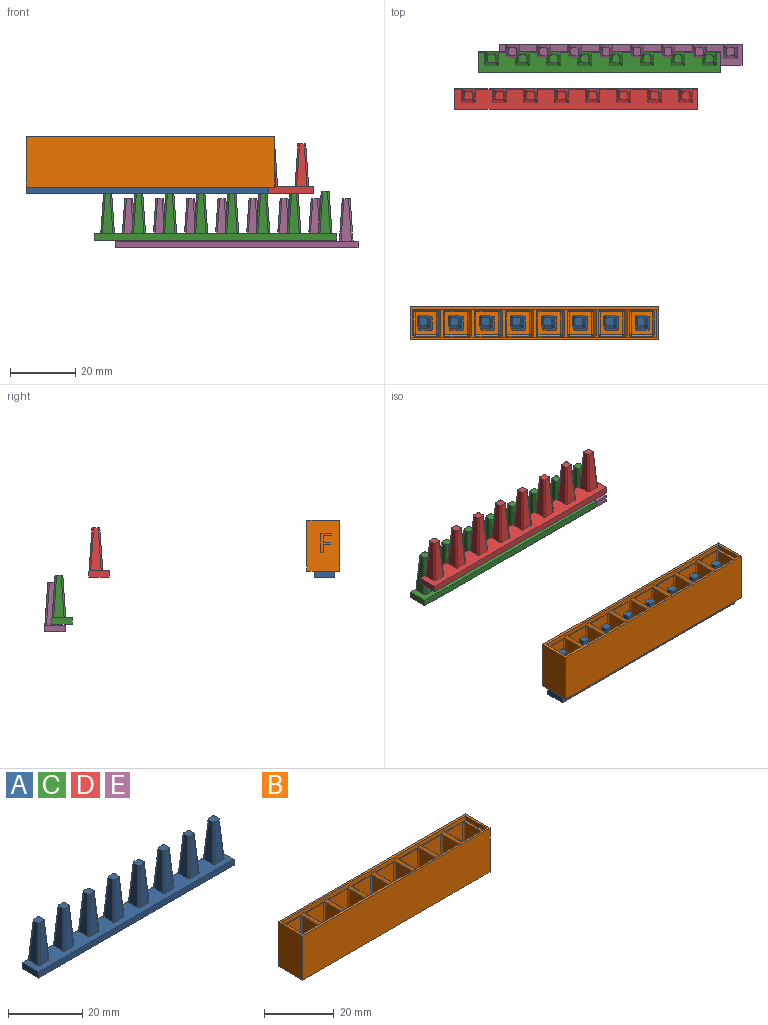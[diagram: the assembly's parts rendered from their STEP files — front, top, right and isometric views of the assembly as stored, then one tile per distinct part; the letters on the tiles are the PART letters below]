
ASSEMBLY  parts=5 mates=2
PART A: 78 faces, bbox 74.2x6.3x15 mm
  f0: plane 13x3.2mm, normal (-1,0,0.07), area 29.9mm2, adj f4,f5,f8,f9
  f1: plane 13x3.2mm, normal (0,-1,0.07), area 29.9mm2, adj f4,f5,f6,f9
  f2: plane 13x3.2mm, normal (1,0,0.07), area 29.9mm2, adj f4,f6,f7,f9
  f3: plane 13x3.2mm, normal (0,1,0.07), area 29.9mm2, adj f4,f7,f8,f74
  f4: plane 2.38x2.38mm, normal (0,0,1), area 5.5mm2, adj f0,f1,f2,f3,f5,f6,f7,f8
  f5: cylinder r=0.5mm len=13.03mm, axis (-0.07,-0.07,-1), area 10.2mm2, adj f0,f1,f4,f9
  f6: cylinder r=0.5mm len=13.03mm, axis (0.07,-0.07,-1), area 10.2mm2, adj f1,f2,f4,f9
  f7: cylinder r=0.5mm len=13.03mm, axis (0.07,0.07,-1), area 10.2mm2, adj f2,f3,f4,f9
  f8: cylinder r=0.5mm len=13.03mm, axis (-0.07,0.07,-1), area 10.2mm2, adj f0,f3,f4,f9
  f9: plane 74.2x6.2mm, normal (0,0,1), area 320.6mm2, adj f0,f1,f2,f5,f6,f7,f8,f11
  f10: plane 13x3.2mm, normal (0,1,0.07), area 29.9mm2, adj f14,f15,f18,f74
  f11: plane 13x3.2mm, normal (-1,0,0.07), area 29.9mm2, adj f9,f14,f15,f16
  f12: plane 13x3.2mm, normal (0,-1,0.07), area 29.9mm2, adj f9,f14,f16,f17
  f13: plane 13x3.2mm, normal (1,0,0.07), area 29.9mm2, adj f9,f14,f17,f18
  f14: plane 2.38x2.38mm, normal (0,0,1), area 5.5mm2, adj f10,f11,f12,f13,f15,f16,f17,f18
  f15: cylinder r=0.5mm len=13.03mm, axis (-0.07,0.07,-1), area 10.2mm2, adj f9,f10,f11,f14
  f16: cylinder r=0.5mm len=13.03mm, axis (-0.07,-0.07,-1), area 10.2mm2, adj f9,f11,f12,f14
  f17: cylinder r=0.5mm len=13.03mm, axis (0.07,-0.07,-1), area 10.2mm2, adj f9,f12,f13,f14
  f18: cylinder r=0.5mm len=13.03mm, axis (0.07,0.07,-1), area 10.2mm2, adj f9,f10,f13,f14
  f19: plane 13x3.2mm, normal (0,1,0.07), area 29.9mm2, adj f23,f24,f27,f74
  f20: plane 13x3.2mm, normal (-1,0,0.07), area 29.9mm2, adj f9,f23,f24,f25
  f21: plane 13x3.2mm, normal (0,-1,0.07), area 29.9mm2, adj f9,f23,f25,f26
  f22: plane 13x3.2mm, normal (1,0,0.07), area 29.9mm2, adj f9,f23,f26,f27
  f23: plane 2.38x2.38mm, normal (0,0,1), area 5.5mm2, adj f19,f20,f21,f22,f24,f25,f26,f27
  f24: cylinder r=0.5mm len=13.03mm, axis (-0.07,0.07,-1), area 10.2mm2, adj f9,f19,f20,f23
  f25: cylinder r=0.5mm len=13.03mm, axis (-0.07,-0.07,-1), area 10.2mm2, adj f9,f20,f21,f23
  f26: cylinder r=0.5mm len=13.03mm, axis (0.07,-0.07,-1), area 10.2mm2, adj f9,f21,f22,f23
  f27: cylinder r=0.5mm len=13.03mm, axis (0.07,0.07,-1), area 10.2mm2, adj f9,f19,f22,f23
  f28: plane 13x3.2mm, normal (0,1,0.07), area 29.9mm2, adj f32,f33,f36,f74
  f29: plane 13x3.2mm, normal (-1,0,0.07), area 29.9mm2, adj f9,f32,f33,f34
  f30: plane 13x3.2mm, normal (0,-1,0.07), area 29.9mm2, adj f9,f32,f34,f35
  f31: plane 13x3.2mm, normal (1,0,0.07), area 29.9mm2, adj f9,f32,f35,f36
  f32: plane 2.38x2.38mm, normal (0,0,1), area 5.5mm2, adj f28,f29,f30,f31,f33,f34,f35,f36
  f33: cylinder r=0.5mm len=13.03mm, axis (-0.07,0.07,-1), area 10.2mm2, adj f9,f28,f29,f32
  f34: cylinder r=0.5mm len=13.03mm, axis (-0.07,-0.07,-1), area 10.2mm2, adj f9,f29,f30,f32
  f35: cylinder r=0.5mm len=13.03mm, axis (0.07,-0.07,-1), area 10.2mm2, adj f9,f30,f31,f32
  f36: cylinder r=0.5mm len=13.03mm, axis (0.07,0.07,-1), area 10.2mm2, adj f9,f28,f31,f32
  f37: plane 13x3.2mm, normal (0,1,0.07), area 29.9mm2, adj f41,f42,f45,f74
  f38: plane 13x3.2mm, normal (-1,0,0.07), area 29.9mm2, adj f9,f41,f42,f43
  f39: plane 13x3.2mm, normal (0,-1,0.07), area 29.9mm2, adj f9,f41,f43,f44
  f40: plane 13x3.2mm, normal (1,0,0.07), area 29.9mm2, adj f9,f41,f44,f45
  f41: plane 2.38x2.38mm, normal (0,0,1), area 5.5mm2, adj f37,f38,f39,f40,f42,f43,f44,f45
  f42: cylinder r=0.5mm len=13.03mm, axis (-0.07,0.07,-1), area 10.2mm2, adj f9,f37,f38,f41
  f43: cylinder r=0.5mm len=13.03mm, axis (-0.07,-0.07,-1), area 10.2mm2, adj f9,f38,f39,f41
  f44: cylinder r=0.5mm len=13.03mm, axis (0.07,-0.07,-1), area 10.2mm2, adj f9,f39,f40,f41
  f45: cylinder r=0.5mm len=13.03mm, axis (0.07,0.07,-1), area 10.2mm2, adj f9,f37,f40,f41
  f46: plane 13x3.2mm, normal (0,1,0.07), area 29.9mm2, adj f50,f51,f54,f74
  f47: plane 13x3.2mm, normal (-1,0,0.07), area 29.9mm2, adj f9,f50,f51,f52
  f48: plane 13x3.2mm, normal (0,-1,0.07), area 29.9mm2, adj f9,f50,f52,f53
  f49: plane 13x3.2mm, normal (1,0,0.07), area 29.9mm2, adj f9,f50,f53,f54
  f50: plane 2.38x2.38mm, normal (0,0,1), area 5.5mm2, adj f46,f47,f48,f49,f51,f52,f53,f54
  f51: cylinder r=0.5mm len=13.03mm, axis (-0.07,0.07,-1), area 10.2mm2, adj f9,f46,f47,f50
  f52: cylinder r=0.5mm len=13.03mm, axis (-0.07,-0.07,-1), area 10.2mm2, adj f9,f47,f48,f50
  f53: cylinder r=0.5mm len=13.03mm, axis (0.07,-0.07,-1), area 10.2mm2, adj f9,f48,f49,f50
  f54: cylinder r=0.5mm len=13.03mm, axis (0.07,0.07,-1), area 10.2mm2, adj f9,f46,f49,f50
  f55: plane 13x3.2mm, normal (0,1,0.07), area 29.9mm2, adj f59,f60,f63,f74
  f56: plane 13x3.2mm, normal (-1,0,0.07), area 29.9mm2, adj f9,f59,f60,f61
  f57: plane 13x3.2mm, normal (0,-1,0.07), area 29.9mm2, adj f9,f59,f61,f62
  f58: plane 13x3.2mm, normal (1,0,0.07), area 29.9mm2, adj f9,f59,f62,f63
  f59: plane 2.38x2.38mm, normal (0,0,1), area 5.5mm2, adj f55,f56,f57,f58,f60,f61,f62,f63
  f60: cylinder r=0.5mm len=13.03mm, axis (-0.07,0.07,-1), area 10.2mm2, adj f9,f55,f56,f59
  f61: cylinder r=0.5mm len=13.03mm, axis (-0.07,-0.07,-1), area 10.2mm2, adj f9,f56,f57,f59
  f62: cylinder r=0.5mm len=13.03mm, axis (0.07,-0.07,-1), area 10.2mm2, adj f9,f57,f58,f59
  f63: cylinder r=0.5mm len=13.03mm, axis (0.07,0.07,-1), area 10.2mm2, adj f9,f55,f58,f59
  f64: plane 13x3.2mm, normal (0,1,0.07), area 29.9mm2, adj f68,f69,f72,f74
  f65: plane 13x3.2mm, normal (-1,0,0.07), area 29.9mm2, adj f9,f68,f69,f70
  f66: plane 13x3.2mm, normal (0,-1,0.07), area 29.9mm2, adj f9,f68,f70,f71
  f67: plane 13x3.2mm, normal (1,0,0.07), area 29.9mm2, adj f9,f68,f71,f72
  f68: plane 2.38x2.38mm, normal (0,0,1), area 5.5mm2, adj f64,f65,f66,f67,f69,f70,f71,f72
  f69: cylinder r=0.5mm len=13.03mm, axis (-0.07,0.07,-1), area 10.2mm2, adj f9,f64,f65,f68
  f70: cylinder r=0.5mm len=13.03mm, axis (-0.07,-0.07,-1), area 10.2mm2, adj f9,f65,f66,f68
  f71: cylinder r=0.5mm len=13.03mm, axis (0.07,-0.07,-1), area 10.2mm2, adj f9,f66,f67,f68
  f72: cylinder r=0.5mm len=13.03mm, axis (0.07,0.07,-1), area 10.2mm2, adj f9,f64,f67,f68
  f73: plane 6.34x2mm, normal (-1,0,0), area 12.5mm2, adj f9,f74,f76,f77
  f74: plane 74.2x2mm, normal (0,1,0.07), area 148.8mm2, adj f3,f9,f10,f19,f28,f37,f46,f55
  f75: plane 6.34x2mm, normal (1,0,0), area 12.5mm2, adj f9,f74,f76,f77
  f76: plane 74.2x2mm, normal (0,-1,0), area 148.4mm2, adj f9,f73,f75,f77
  f77: plane 74.2x6.34mm, normal (0,0,-1), area 470.4mm2, adj f73,f74,f75,f76
PART B: 255 faces, bbox 76x10x15.5 mm
  f0: plane 74.5x1.5mm, normal (0,1,0), area 108.2mm2, adj f1,f2,f3,f4,f5,f6,f7,f51
  f1: plane 8.5x8.09mm, normal (0,0,1), area 4.9mm2, adj f0,f21,f22,f23,f42,f213,f215,f218
  f2: plane 8.5x8.09mm, normal (0,0,1), area 4.9mm2, adj f0,f24,f25,f26,f43,f201,f203,f206
  f3: plane 8.5x8.09mm, normal (0,0,1), area 4.9mm2, adj f0,f27,f28,f29,f44,f189,f191,f194
  f4: plane 8.5x8.09mm, normal (0,0,1), area 4.9mm2, adj f0,f30,f31,f32,f45,f177,f179,f182
  f5: plane 8.5x8.09mm, normal (0,0,1), area 4.9mm2, adj f0,f33,f34,f35,f46,f165,f167,f170
  f6: plane 8.5x8.09mm, normal (0,0,1), area 4.9mm2, adj f0,f36,f37,f38,f47,f153,f155,f158
  f7: plane 8.5x7.79mm, normal (0,0,1), area 6.5mm2, adj f0,f8,f9,f49,f116,f141,f142,f147
  f8: plane 11.5x6.5mm, normal (0,1,0), area 74.8mm2, adj f7,f141,f146,f147
  f9: plane 11.5x6.5mm, normal (0,-1,0), area 74.8mm2, adj f7,f142,f148,f149
  f10: plane 7x6.5mm, normal (0,0,1), area 27mm2, adj f80,f81,f82,f83,f112,f113,f114,f115
  f11: plane 7x6.5mm, normal (0,0,1), area 27mm2, adj f52,f53,f54,f55,f84,f85,f86,f87
  f12: plane 7x7mm, normal (0,0,1), area 30.5mm2, adj f76,f77,f78,f79,f108,f109,f110,f111
  f13: plane 7x7mm, normal (0,0,1), area 30.5mm2, adj f72,f73,f74,f75,f104,f105,f106,f107
  f14: plane 7x7mm, normal (0,0,1), area 30.5mm2, adj f68,f69,f70,f71,f100,f101,f102,f103
  f15: plane 7x7mm, normal (0,0,1), area 30.5mm2, adj f64,f65,f66,f67,f96,f97,f98,f99
  f16: plane 7x7mm, normal (0,0,1), area 30.5mm2, adj f60,f61,f62,f63,f92,f93,f94,f95
  f17: plane 7x7mm, normal (0,0,1), area 30.5mm2, adj f56,f57,f58,f59,f88,f89,f90,f91
  f18: plane 76x10mm, normal (0,0,-1), area 592.4mm2, adj f39,f40,f41,f48,f52,f53,f54,f55
  f19: plane 11.5x7mm, normal (1,0,0), area 80.5mm2, adj f51,f129,f130,f131
  f20: plane 11.5x6.5mm, normal (0,-1,0), area 74.7mm2, adj f51,f131,f136,f137
  f21: plane 11.5x7mm, normal (1,0,0), area 80.5mm2, adj f1,f218,f222,f224
  f22: plane 11.5x7mm, normal (0,-1,0), area 80.5mm2, adj f1,f215,f221,f224
  f23: plane 11.5x7mm, normal (-1,0,0), area 80.5mm2, adj f1,f213,f215,f216
  f24: plane 11.5x7mm, normal (1,0,0), area 80.5mm2, adj f2,f206,f210,f212
  f25: plane 11.5x7mm, normal (0,-1,0), area 80.5mm2, adj f2,f203,f209,f212
  f26: plane 11.5x7mm, normal (-1,0,0), area 80.5mm2, adj f2,f201,f203,f204
  f27: plane 11.5x7mm, normal (1,0,0), area 80.5mm2, adj f3,f194,f198,f200
  f28: plane 11.5x7mm, normal (0,-1,0), area 80.5mm2, adj f3,f191,f197,f200
  f29: plane 11.5x7mm, normal (-1,0,0), area 80.5mm2, adj f3,f189,f191,f192
  f30: plane 11.5x7mm, normal (1,0,0), area 80.5mm2, adj f4,f182,f186,f188
  f31: plane 11.5x7mm, normal (0,-1,0), area 80.5mm2, adj f4,f179,f185,f188
  f32: plane 11.5x7mm, normal (-1,0,0), area 80.5mm2, adj f4,f177,f179,f180
  f33: plane 11.5x7mm, normal (1,0,0), area 80.5mm2, adj f5,f170,f174,f176
  f34: plane 11.5x7mm, normal (0,-1,0), area 80.5mm2, adj f5,f167,f173,f176
  f35: plane 11.5x7mm, normal (-1,0,0), area 80.5mm2, adj f5,f165,f167,f168
  f36: plane 11.5x7mm, normal (1,0,0), area 80.5mm2, adj f6,f158,f162,f164
  f37: plane 11.5x7mm, normal (0,-1,0), area 80.5mm2, adj f6,f155,f161,f164
  f38: plane 11.5x7mm, normal (-1,0,0), area 80.5mm2, adj f6,f153,f155,f156
  f39: plane 76x15.5mm, normal (0,-1,0), area 1178mm2, adj f18,f40,f48,f228
  f40: plane 15.5x10mm, normal (1,0,0), area 155mm2, adj f18,f39,f41,f228
  f41: plane 76x15.5mm, normal (0,1,0), area 1178mm2, adj f18,f40,f48,f228
  f42: plane 11.5x7mm, normal (0,1,0), area 80.5mm2, adj f1,f213,f217,f218
  f43: plane 11.5x7mm, normal (0,1,0), area 80.5mm2, adj f2,f201,f205,f206
  f44: plane 11.5x7mm, normal (0,1,0), area 80.5mm2, adj f3,f189,f193,f194
  f45: plane 11.5x7mm, normal (0,1,0), area 80.5mm2, adj f4,f177,f181,f182
  f46: plane 11.5x7mm, normal (0,1,0), area 80.5mm2, adj f5,f165,f169,f170
  f47: plane 11.5x7mm, normal (0,1,0), area 80.5mm2, adj f6,f153,f157,f158
  f48: plane 15.5x10mm, normal (-1,0,0), area 155mm2, adj f18,f39,f41,f228
  f49: plane 11.5x7mm, normal (-1,0,0), area 80.5mm2, adj f7,f141,f142,f143
  f50: plane 11.5x6.5mm, normal (0,1,0), area 74.7mm2, adj f51,f129,f134,f135
  f51: plane 8.5x8.29mm, normal (0,0,1), area 10.7mm2, adj f0,f19,f20,f50,f117,f129,f131,f134
  f52: plane 3.6x2mm, normal (0,1,-0.07), area 6.9mm2, adj f11,f18,f84,f87
  f53: plane 3.6x2mm, normal (1,0,-0.07), area 6.9mm2, adj f11,f18,f86,f87
  f54: plane 3.6x2mm, normal (0,-1,-0.07), area 6.9mm2, adj f11,f18,f85,f86
  f55: plane 3.6x2mm, normal (-1,0,-0.07), area 6.9mm2, adj f11,f18,f84,f85
  f56: plane 3.6x2mm, normal (0,1,-0.07), area 6.9mm2, adj f17,f18,f88,f91
  f57: plane 3.6x2mm, normal (1,0,-0.07), area 6.9mm2, adj f17,f18,f90,f91
  f58: plane 3.6x2mm, normal (0,-1,-0.07), area 6.9mm2, adj f17,f18,f89,f90
  f59: plane 3.6x2mm, normal (-1,0,-0.07), area 6.9mm2, adj f17,f18,f88,f89
  f60: plane 3.6x2mm, normal (0,1,-0.07), area 6.9mm2, adj f16,f18,f92,f95
  f61: plane 3.6x2mm, normal (1,0,-0.07), area 6.9mm2, adj f16,f18,f94,f95
  f62: plane 3.6x2mm, normal (0,-1,-0.07), area 6.9mm2, adj f16,f18,f93,f94
  f63: plane 3.6x2mm, normal (-1,0,-0.07), area 6.9mm2, adj f16,f18,f92,f93
  f64: plane 3.6x2mm, normal (0,1,-0.07), area 6.9mm2, adj f15,f18,f96,f99
  f65: plane 3.6x2mm, normal (1,0,-0.07), area 6.9mm2, adj f15,f18,f98,f99
  f66: plane 3.6x2mm, normal (0,-1,-0.07), area 6.9mm2, adj f15,f18,f97,f98
  f67: plane 3.6x2mm, normal (-1,0,-0.07), area 6.9mm2, adj f15,f18,f96,f97
  f68: plane 3.6x2mm, normal (0,1,-0.07), area 6.9mm2, adj f14,f18,f100,f103
  f69: plane 3.6x2mm, normal (1,0,-0.07), area 6.9mm2, adj f14,f18,f102,f103
  f70: plane 3.6x2mm, normal (0,-1,-0.07), area 6.9mm2, adj f14,f18,f101,f102
  f71: plane 3.6x2mm, normal (-1,0,-0.07), area 6.9mm2, adj f14,f18,f100,f101
  f72: plane 3.6x2mm, normal (0,1,-0.07), area 6.9mm2, adj f13,f18,f104,f107
  f73: plane 3.6x2mm, normal (1,0,-0.07), area 6.9mm2, adj f13,f18,f106,f107
  f74: plane 3.6x2mm, normal (0,-1,-0.07), area 6.9mm2, adj f13,f18,f105,f106
  f75: plane 3.6x2mm, normal (-1,0,-0.07), area 6.9mm2, adj f13,f18,f104,f105
  f76: plane 3.6x2mm, normal (0,1,-0.07), area 6.9mm2, adj f12,f18,f108,f111
  f77: plane 3.6x2mm, normal (1,0,-0.07), area 6.9mm2, adj f12,f18,f108,f109
  f78: plane 3.6x2mm, normal (0,-1,-0.07), area 6.9mm2, adj f12,f18,f109,f110
  f79: plane 3.6x2mm, normal (-1,0,-0.07), area 6.9mm2, adj f12,f18,f110,f111
  f80: plane 3.6x2mm, normal (1,0,-0.07), area 6.9mm2, adj f10,f18,f112,f115
  f81: plane 3.6x2mm, normal (0,-1,-0.07), area 6.9mm2, adj f10,f18,f114,f115
  f82: plane 3.6x2mm, normal (-1,0,-0.07), area 6.9mm2, adj f10,f18,f113,f114
  f83: plane 3.6x2mm, normal (0,1,-0.07), area 6.9mm2, adj f10,f18,f112,f113
  f84: cylinder r=0.5mm len=2.03mm, axis (-0.07,0.07,1), area 1.6mm2, adj f11,f18,f52,f55
  f85: cylinder r=0.5mm len=2.03mm, axis (-0.07,-0.07,1), area 1.6mm2, adj f11,f18,f54,f55
  f86: cylinder r=0.5mm len=2.03mm, axis (0.07,-0.07,1), area 1.6mm2, adj f11,f18,f53,f54
  f87: cylinder r=0.5mm len=2.03mm, axis (0.07,0.07,1), area 1.6mm2, adj f11,f18,f52,f53
  f88: cylinder r=0.5mm len=2.03mm, axis (-0.07,0.07,1), area 1.6mm2, adj f17,f18,f56,f59
  f89: cylinder r=0.5mm len=2.03mm, axis (-0.07,-0.07,1), area 1.6mm2, adj f17,f18,f58,f59
  f90: cylinder r=0.5mm len=2.03mm, axis (0.07,-0.07,1), area 1.6mm2, adj f17,f18,f57,f58
  f91: cylinder r=0.5mm len=2.03mm, axis (0.07,0.07,1), area 1.6mm2, adj f17,f18,f56,f57
  f92: cylinder r=0.5mm len=2.03mm, axis (-0.07,0.07,1), area 1.6mm2, adj f16,f18,f60,f63
  f93: cylinder r=0.5mm len=2.03mm, axis (-0.07,-0.07,1), area 1.6mm2, adj f16,f18,f62,f63
  f94: cylinder r=0.5mm len=2.03mm, axis (0.07,-0.07,1), area 1.6mm2, adj f16,f18,f61,f62
  f95: cylinder r=0.5mm len=2.03mm, axis (0.07,0.07,1), area 1.6mm2, adj f16,f18,f60,f61
  f96: cylinder r=0.5mm len=2.03mm, axis (-0.07,0.07,1), area 1.6mm2, adj f15,f18,f64,f67
  f97: cylinder r=0.5mm len=2.03mm, axis (-0.07,-0.07,1), area 1.6mm2, adj f15,f18,f66,f67
  f98: cylinder r=0.5mm len=2.03mm, axis (0.07,-0.07,1), area 1.6mm2, adj f15,f18,f65,f66
  f99: cylinder r=0.5mm len=2.03mm, axis (0.07,0.07,1), area 1.6mm2, adj f15,f18,f64,f65
  f100: cylinder r=0.5mm len=2.03mm, axis (-0.07,0.07,1), area 1.6mm2, adj f14,f18,f68,f71
  f101: cylinder r=0.5mm len=2.03mm, axis (-0.07,-0.07,1), area 1.6mm2, adj f14,f18,f70,f71
  f102: cylinder r=0.5mm len=2.03mm, axis (0.07,-0.07,1), area 1.6mm2, adj f14,f18,f69,f70
  f103: cylinder r=0.5mm len=2.03mm, axis (0.07,0.07,1), area 1.6mm2, adj f14,f18,f68,f69
  f104: cylinder r=0.5mm len=2.03mm, axis (-0.07,0.07,1), area 1.6mm2, adj f13,f18,f72,f75
  f105: cylinder r=0.5mm len=2.03mm, axis (-0.07,-0.07,1), area 1.6mm2, adj f13,f18,f74,f75
  f106: cylinder r=0.5mm len=2.03mm, axis (0.07,-0.07,1), area 1.6mm2, adj f13,f18,f73,f74
  f107: cylinder r=0.5mm len=2.03mm, axis (0.07,0.07,1), area 1.6mm2, adj f13,f18,f72,f73
  f108: cylinder r=0.5mm len=2.03mm, axis (0.07,0.07,1), area 1.6mm2, adj f12,f18,f76,f77
  f109: cylinder r=0.5mm len=2.03mm, axis (0.07,-0.07,1), area 1.6mm2, adj f12,f18,f77,f78
  f110: cylinder r=0.5mm len=2.03mm, axis (-0.07,-0.07,1), area 1.6mm2, adj f12,f18,f78,f79
  f111: cylinder r=0.5mm len=2.03mm, axis (-0.07,0.07,1), area 1.6mm2, adj f12,f18,f76,f79
  f112: cylinder r=0.5mm len=2.03mm, axis (0.07,0.07,1), area 1.6mm2, adj f10,f18,f80,f83
  f113: cylinder r=0.5mm len=2.03mm, axis (-0.07,0.07,1), area 1.6mm2, adj f10,f18,f82,f83
  f114: cylinder r=0.5mm len=2.03mm, axis (-0.07,-0.07,1), area 1.6mm2, adj f10,f18,f81,f82
  f115: cylinder r=0.5mm len=2.03mm, axis (0.07,-0.07,1), area 1.6mm2, adj f10,f18,f80,f81
  f116: plane 11.5x7mm, normal (1,0,0), area 73.7mm2, adj f7,f118,f119,f120,f121,f122,f123,f124
  f117: plane 11.5x7mm, normal (-1,0,0), area 80.5mm2, adj f51,f134,f137,f140
  f118: plane 2.46x0.6mm, normal (0,1,0), area 1.5mm2, adj f116,f119,f127,f128
  f119: plane 2.39x0.6mm, normal (0,0,1), area 1.4mm2, adj f116,f118,f120,f128
  f120: plane 0.6x0.6mm, normal (0,1,0), area 0.4mm2, adj f116,f119,f121,f128
  f121: plane 2.39x0.6mm, normal (0,0,-1), area 1.4mm2, adj f116,f120,f122,f128
  f122: plane 2.11x0.6mm, normal (0,1,0), area 1.3mm2, adj f116,f121,f123,f128
  f123: plane 2.54x0.6mm, normal (0,0,1), area 1.5mm2, adj f116,f122,f124,f128
  f124: plane 0.6x0.6mm, normal (0,1,0), area 0.4mm2, adj f116,f123,f125,f128
  f125: plane 3.21x0.6mm, normal (0,0,-1), area 1.9mm2, adj f116,f124,f126,f128
  f126: plane 5.76x0.6mm, normal (0,-1,0), area 3.5mm2, adj f116,f125,f127,f128
  f127: plane 0.67x0.6mm, normal (0,0,1), area 0.4mm2, adj f116,f118,f126,f128
  f128: plane 5.76x3.21mm, normal (1,0,0), area 6.8mm2, adj f118,f119,f120,f121,f122,f123,f124,f125
  f129: cylinder r=0.5mm len=11.5mm, axis (0,0,1), area 9mm2, adj f19,f50,f51,f132
  f130: cylinder r=0.5mm len=7mm, axis (0,-1,0), area 5.5mm2, adj f11,f19,f132,f133
  f131: cylinder r=0.5mm len=11.5mm, axis (0,0,-1), area 9mm2, adj f19,f20,f51,f133
  f132: sphere r=0.5mm, area 0.4mm2, adj f129,f130,f135
  f133: sphere r=0.5mm, area 0.4mm2, adj f130,f131,f136
  f134: cylinder r=0.5mm len=11.5mm, axis (0,0,-1), area 9mm2, adj f50,f51,f117,f138
  f135: cylinder r=0.5mm len=6.5mm, axis (1,0,0), area 5.1mm2, adj f11,f50,f132,f138
  f136: cylinder r=0.5mm len=6.5mm, axis (-1,0,0), area 5.1mm2, adj f11,f20,f133,f139
  f137: cylinder r=0.5mm len=11.5mm, axis (0,0,1), area 9mm2, adj f20,f51,f117,f139
  f138: sphere r=0.5mm, area 0.4mm2, adj f134,f135,f140
  f139: sphere r=0.5mm, area 0.4mm2, adj f136,f137,f140
  f140: cylinder r=0.5mm len=7mm, axis (0,1,0), area 5.5mm2, adj f11,f117,f138,f139
  f141: cylinder r=0.5mm len=11.5mm, axis (0,0,-1), area 9mm2, adj f7,f8,f49,f144
  f142: cylinder r=0.5mm len=11.5mm, axis (0,0,1), area 9mm2, adj f7,f9,f49,f145
  f143: cylinder r=0.5mm len=7mm, axis (0,1,0), area 5.5mm2, adj f10,f49,f144,f145
  f144: sphere r=0.5mm, area 0.4mm2, adj f141,f143,f146
  f145: sphere r=0.5mm, area 0.4mm2, adj f142,f143,f149
  f146: cylinder r=0.5mm len=6.5mm, axis (1,0,0), area 5.1mm2, adj f8,f10,f144,f150
  f147: cylinder r=0.5mm len=11.5mm, axis (0,0,1), area 9mm2, adj f7,f8,f116,f150
  f148: cylinder r=0.5mm len=11.5mm, axis (0,0,-1), area 9mm2, adj f7,f9,f116,f151
  f149: cylinder r=0.5mm len=6.5mm, axis (-1,0,0), area 5.1mm2, adj f9,f10,f145,f151
  f150: sphere r=0.5mm, area 0.4mm2, adj f146,f147,f152
  f151: sphere r=0.5mm, area 0.4mm2, adj f148,f149,f152
  f152: cylinder r=0.5mm len=7mm, axis (0,-1,0), area 5.5mm2, adj f10,f116,f150,f151
  f153: cylinder r=0.5mm len=11.5mm, axis (0,0,-1), area 9mm2, adj f6,f38,f47,f154
  f154: sphere r=0.5mm, area 0.4mm2, adj f153,f156,f157
  f155: cylinder r=0.5mm len=11.5mm, axis (0,0,1), area 9mm2, adj f6,f37,f38,f159
  f156: cylinder r=0.5mm len=7mm, axis (0,1,0), area 5.5mm2, adj f12,f38,f154,f159
  f157: cylinder r=0.5mm len=7mm, axis (1,0,0), area 5.5mm2, adj f12,f47,f154,f160
  f158: cylinder r=0.5mm len=11.5mm, axis (0,0,1), area 9mm2, adj f6,f36,f47,f160
  f159: sphere r=0.5mm, area 0.4mm2, adj f155,f156,f161
  f160: sphere r=0.5mm, area 0.4mm2, adj f157,f158,f162
  f161: cylinder r=0.5mm len=7mm, axis (-1,0,0), area 5.5mm2, adj f12,f37,f159,f163
  f162: cylinder r=0.5mm len=7mm, axis (0,-1,0), area 5.5mm2, adj f12,f36,f160,f163
  f163: sphere r=0.5mm, area 0.4mm2, adj f161,f162,f164
  f164: cylinder r=0.5mm len=11.5mm, axis (0,0,-1), area 9mm2, adj f6,f36,f37,f163
  f165: cylinder r=0.5mm len=11.5mm, axis (0,0,-1), area 9mm2, adj f5,f35,f46,f166
  f166: sphere r=0.5mm, area 0.4mm2, adj f165,f168,f169
  f167: cylinder r=0.5mm len=11.5mm, axis (0,0,1), area 9mm2, adj f5,f34,f35,f171
  f168: cylinder r=0.5mm len=7mm, axis (0,1,0), area 5.5mm2, adj f13,f35,f166,f171
  f169: cylinder r=0.5mm len=7mm, axis (1,0,0), area 5.5mm2, adj f13,f46,f166,f172
  f170: cylinder r=0.5mm len=11.5mm, axis (0,0,1), area 9mm2, adj f5,f33,f46,f172
  f171: sphere r=0.5mm, area 0.4mm2, adj f167,f168,f173
  f172: sphere r=0.5mm, area 0.4mm2, adj f169,f170,f174
  f173: cylinder r=0.5mm len=7mm, axis (-1,0,0), area 5.5mm2, adj f13,f34,f171,f175
  f174: cylinder r=0.5mm len=7mm, axis (0,-1,0), area 5.5mm2, adj f13,f33,f172,f175
  f175: sphere r=0.5mm, area 0.4mm2, adj f173,f174,f176
  f176: cylinder r=0.5mm len=11.5mm, axis (0,0,-1), area 9mm2, adj f5,f33,f34,f175
  f177: cylinder r=0.5mm len=11.5mm, axis (0,0,-1), area 9mm2, adj f4,f32,f45,f178
  f178: sphere r=0.5mm, area 0.4mm2, adj f177,f180,f181
  f179: cylinder r=0.5mm len=11.5mm, axis (0,0,1), area 9mm2, adj f4,f31,f32,f183
  f180: cylinder r=0.5mm len=7mm, axis (0,1,0), area 5.5mm2, adj f14,f32,f178,f183
  f181: cylinder r=0.5mm len=7mm, axis (1,0,0), area 5.5mm2, adj f14,f45,f178,f184
  f182: cylinder r=0.5mm len=11.5mm, axis (0,0,1), area 9mm2, adj f4,f30,f45,f184
  f183: sphere r=0.5mm, area 0.4mm2, adj f179,f180,f185
  f184: sphere r=0.5mm, area 0.4mm2, adj f181,f182,f186
  f185: cylinder r=0.5mm len=7mm, axis (-1,0,0), area 5.5mm2, adj f14,f31,f183,f187
  f186: cylinder r=0.5mm len=7mm, axis (0,-1,0), area 5.5mm2, adj f14,f30,f184,f187
  f187: sphere r=0.5mm, area 0.4mm2, adj f185,f186,f188
  f188: cylinder r=0.5mm len=11.5mm, axis (0,0,-1), area 9mm2, adj f4,f30,f31,f187
  f189: cylinder r=0.5mm len=11.5mm, axis (0,0,-1), area 9mm2, adj f3,f29,f44,f190
  f190: sphere r=0.5mm, area 0.4mm2, adj f189,f192,f193
  f191: cylinder r=0.5mm len=11.5mm, axis (0,0,1), area 9mm2, adj f3,f28,f29,f195
  f192: cylinder r=0.5mm len=7mm, axis (0,1,0), area 5.5mm2, adj f15,f29,f190,f195
  f193: cylinder r=0.5mm len=7mm, axis (1,0,0), area 5.5mm2, adj f15,f44,f190,f196
  f194: cylinder r=0.5mm len=11.5mm, axis (0,0,1), area 9mm2, adj f3,f27,f44,f196
  f195: sphere r=0.5mm, area 0.4mm2, adj f191,f192,f197
  f196: sphere r=0.5mm, area 0.4mm2, adj f193,f194,f198
  f197: cylinder r=0.5mm len=7mm, axis (-1,0,0), area 5.5mm2, adj f15,f28,f195,f199
  f198: cylinder r=0.5mm len=7mm, axis (0,-1,0), area 5.5mm2, adj f15,f27,f196,f199
  f199: sphere r=0.5mm, area 0.4mm2, adj f197,f198,f200
  f200: cylinder r=0.5mm len=11.5mm, axis (0,0,-1), area 9mm2, adj f3,f27,f28,f199
  f201: cylinder r=0.5mm len=11.5mm, axis (0,0,-1), area 9mm2, adj f2,f26,f43,f202
  f202: sphere r=0.5mm, area 0.4mm2, adj f201,f204,f205
  f203: cylinder r=0.5mm len=11.5mm, axis (0,0,1), area 9mm2, adj f2,f25,f26,f207
  f204: cylinder r=0.5mm len=7mm, axis (0,1,0), area 5.5mm2, adj f16,f26,f202,f207
  f205: cylinder r=0.5mm len=7mm, axis (1,0,0), area 5.5mm2, adj f16,f43,f202,f208
  f206: cylinder r=0.5mm len=11.5mm, axis (0,0,1), area 9mm2, adj f2,f24,f43,f208
  f207: sphere r=0.5mm, area 0.4mm2, adj f203,f204,f209
  f208: sphere r=0.5mm, area 0.4mm2, adj f205,f206,f210
  f209: cylinder r=0.5mm len=7mm, axis (-1,0,0), area 5.5mm2, adj f16,f25,f207,f211
  f210: cylinder r=0.5mm len=7mm, axis (0,-1,0), area 5.5mm2, adj f16,f24,f208,f211
  f211: sphere r=0.5mm, area 0.4mm2, adj f209,f210,f212
  f212: cylinder r=0.5mm len=11.5mm, axis (0,0,-1), area 9mm2, adj f2,f24,f25,f211
  f213: cylinder r=0.5mm len=11.5mm, axis (0,0,-1), area 9mm2, adj f1,f23,f42,f214
  f214: sphere r=0.5mm, area 0.4mm2, adj f213,f216,f217
  f215: cylinder r=0.5mm len=11.5mm, axis (0,0,1), area 9mm2, adj f1,f22,f23,f219
  f216: cylinder r=0.5mm len=7mm, axis (0,1,0), area 5.5mm2, adj f17,f23,f214,f219
  f217: cylinder r=0.5mm len=7mm, axis (1,0,0), area 5.5mm2, adj f17,f42,f214,f220
  f218: cylinder r=0.5mm len=11.5mm, axis (0,0,1), area 9mm2, adj f1,f21,f42,f220
  f219: sphere r=0.5mm, area 0.4mm2, adj f215,f216,f221
  f220: sphere r=0.5mm, area 0.4mm2, adj f217,f218,f222
  f221: cylinder r=0.5mm len=7mm, axis (-1,0,0), area 5.5mm2, adj f17,f22,f219,f223
  f222: cylinder r=0.5mm len=7mm, axis (0,-1,0), area 5.5mm2, adj f17,f21,f220,f223
  f223: sphere r=0.5mm, area 0.4mm2, adj f221,f222,f224
  f224: cylinder r=0.5mm len=11.5mm, axis (0,0,-1), area 9mm2, adj f1,f21,f22,f223
  f225: plane 8.5x1.5mm, normal (1,0,0), area 12.7mm2, adj f0,f7,f226,f228
  f226: plane 74.5x1.5mm, normal (0,-1,0), area 108.2mm2, adj f1,f2,f3,f4,f5,f6,f7,f51
  f227: plane 8.5x1.5mm, normal (-1,0,0), area 12.7mm2, adj f0,f51,f226,f228
  f228: plane 76x10mm, normal (0,0,1), area 126.8mm2, adj f0,f39,f40,f41,f48,f225,f226,f227
  f229: plane 8.5x0.71mm, normal (0.71,0,0.71), area 8.5mm2, adj f0,f6,f226,f230
  f230: plane 8.5x0.71mm, normal (-0.71,0,0.71), area 8.5mm2, adj f0,f7,f226,f229
  f231: plane 8.5x0.71mm, normal (-0.71,0,0.71), area 8.5mm2, adj f0,f6,f226,f232
  f232: plane 8.5x0.71mm, normal (0.71,0,0.71), area 8.5mm2, adj f0,f5,f226,f231
  f233: plane 8.5x0.71mm, normal (-0.71,0,0.71), area 8.5mm2, adj f0,f5,f226,f234
  f234: plane 8.5x0.71mm, normal (0.71,0,0.71), area 8.5mm2, adj f0,f4,f226,f233
  f235: plane 8.5x0.71mm, normal (-0.71,0,0.71), area 8.5mm2, adj f0,f4,f226,f236
  f236: plane 8.5x0.71mm, normal (0.71,0,0.71), area 8.5mm2, adj f0,f3,f226,f235
  f237: plane 8.5x0.71mm, normal (-0.71,0,0.71), area 8.5mm2, adj f0,f3,f226,f238
  f238: plane 8.5x0.71mm, normal (0.71,0,0.71), area 8.5mm2, adj f0,f2,f226,f237
  f239: plane 8.5x0.71mm, normal (-0.71,0,0.71), area 8.5mm2, adj f0,f2,f226,f240
  f240: plane 8.5x0.71mm, normal (0.71,0,0.71), area 8.5mm2, adj f0,f1,f226,f239
  f241: plane 8.5x0.71mm, normal (-0.71,0,0.71), area 8.5mm2, adj f0,f1,f226,f242
  f242: plane 8.5x0.71mm, normal (0.71,0,0.71), area 8.5mm2, adj f0,f51,f226,f241
  f243: plane 2.51x0.6mm, normal (0,-1,0), area 1.5mm2, adj f244,f252,f253,f254
  f244: plane 2.43x0.6mm, normal (0,0,1), area 1.5mm2, adj f243,f245,f253,f254
  f245: plane 0.61x0.6mm, normal (0,-1,0), area 0.4mm2, adj f244,f246,f253,f254
  f246: plane 2.43x0.6mm, normal (0,0,-1), area 1.5mm2, adj f245,f247,f253,f254
  f247: plane 2.15x0.6mm, normal (0,-1,0), area 1.3mm2, adj f246,f248,f253,f254
  f248: plane 2.59x0.6mm, normal (0,0,1), area 1.6mm2, adj f247,f249,f253,f254
  f249: plane 0.61x0.6mm, normal (0,-1,0), area 0.4mm2, adj f248,f250,f253,f254
  f250: plane 3.27x0.6mm, normal (0,0,-1), area 2mm2, adj f249,f251,f253,f254
  f251: plane 5.87x0.6mm, normal (0,1,0), area 3.5mm2, adj f250,f252,f253,f254
  f252: plane 0.68x0.6mm, normal (0,0,1), area 0.4mm2, adj f243,f251,f253,f254
  f253: plane 5.87x3.27mm, normal (-1,0,0), area 7.1mm2, adj f243,f244,f245,f246,f247,f248,f249,f250
  f254: plane 5.87x3.27mm, normal (1,0,0), area 7.1mm2, adj f243,f244,f245,f246,f247,f248,f249,f250
PART C: same geometry as A
PART D: same geometry as A
PART E: same geometry as A
PLACE A t=(-4.86,-75.9,0.45)mm
PLACE B t=(-8.84,-71.43,2.48)mm
PLACE C t=(15.99,4.39,-13.77)mm
PLACE D t=(8.87,-6.94,0.65)mm
PLACE E t=(22.44,6.59,-16.05)mm
MATE parallel A.f2 <-> B.f82  axis (1,0,0.07) through (-3.15,-75.9,6.09)mm
MATE parallel B.f83 <-> A.f1  axis (0,1,-0.07) through (-4.34,-78.66,1.46)mm
